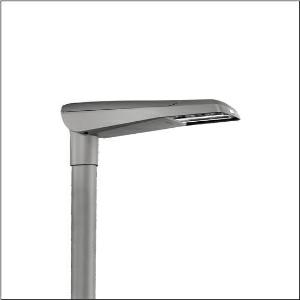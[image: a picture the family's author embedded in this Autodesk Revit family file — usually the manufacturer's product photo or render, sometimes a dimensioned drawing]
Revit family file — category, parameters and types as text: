
# Revit family: streetlight_sl_11_iq_micro___p1_0a_5xc1cc1f08de_50c8
name_source: partatom
category: Lighting Fixtures
units: mm (PartAtom-declared; Revit-internal decimal feet)

## family parameters
Cut with Voids When Loaded = No
Host = Face
Light Source = No
Part Type = Normal
Room Calculation Point = No
Round Connector Dimension = Use Diameter
Shared = No

## types (1)
- --- (1 x LED, 2620 lm, 24.2 W, 2200K)
    Apparent Load = 24 VA
    CIE Flux Codes = 29 63 93 100 100
    Color Rendering = 70
    Color Temperature = 2200K
    Default Elevation = 1800 mm
    Description = Streetlight SL 11 iQ micro, mast luminaire, primary light control with 3 zone facetted reflector, of plastic, silver coated, highly specular, primary optical cover: cover, of PMMA, transparent, light distribution: P1.0a, light emission: direct distribution, primary light characteristic: asymmetric, installation type: post-top, side-entry, lamps: LED, High Power LED, rated values: 3.150lm | 24,1W | 130,7lm/W (begin service life); end service life: 3.150lm | 24,6W; at 50% lumin. flux: 1.575lm | 11,9W | 132,4lm/W, colour temperature: 2200/2700/3000/4000K, colour rendering: CRI > 70, light colour: 722/727/730/740, light setting 1 begin service life: 100% | 3.150lm | 24,1W | 130,7lm/W | 3.000K, light setting 1 end service life: 24,6W, further light settings possible, control: Street-Remote, Auto-Match, Temp-Guard, Lumen-Switch, Night-Set, Smart-Wire, Light-Fading, Desk-Remote (wireless, voltage-free reading and setting of iQ features in the workshop via application-optimized NFC function/RFID function), optimised constant luminous flux control (CLO 2.0), with cable H07RN-F 3x 1.5mm², mains connection: 220..240V, AC, 50/60Hz, connection cable pre-assembled, cable length: 6,5m, luminaire housing, of diecast aluminium, powder-coated, SITECO metallic grey (DB 702S), please order mast flange separately, inclination adjustable without tools: 0°, 5°, 10°, 15° (post-top) | 0°, -5°, -10°, -15° (side-entry), sealing non-destructively replaceable, multi-level sealing system, length: 600mm, width: 174mm, height: 116mm, mast flange for spigot size: 42mm (side-entry): 5XC10008XM4, 60/48mm (side-entry/post-top): 5XC10108XM2, 76/60mm (side-entry/post-top): 5XC10108XM1, equipment: Power, protection rating (complete): IP66, insulation class (complete): insulation class II (safety insulation), certification: CE, ENEC, ENEC+, VDE, impact resistance: IK10, permissible operating ambient temperature for outdoor applications: -25..+50°C, standard-compliant lighting for roads and squares, Environmental Product Declaration (EPD) tested and certified by an independent institute, packaging unit: 1 piece

Light Distribution: P1.0a
    Height = 116 mm
    Lamp = 1 x LED
    Lamp Light Flux = 2620 lm
    Lamp Power = 24.2 W
    Lamp count = 1
    Length = 600 mm
    Luminous efficacy = 108 lm/W
    Manufacturer = Siteco
    ModVariant = No
    Model = 5XC1CC1F08DE
    Mounting Place = Pole
    Mounting Type = Pole top
    Number of Poles = 1
    OnlyDefault = Yes
    Power Factor = 1
    Product Name = Streetlight SL 11 iQ micro | P1.0a
    Product group = mast luminaire | pylon top
    ProductGroupID = 6100
    Protection Class = Protection class II
    Protection Degree = IP 66
    RLX_Detail_Level = 1
    RLX_Emergency_Light_Flux = 0 lm
    RLX_Emergency_Type = 0
    RLX_Emergency_Type_DB = No
    RlxData = <blob elided: 59305 chars, md5=d243c848>
    Socket = socket
    Standby Power = 0 W
    System Light Flux = 2620 lm
    System Power = 24 W
    Type Comments = individual setting: luminous flux: 100 % | dim-lin: 254 | 644 mA
    Type Image = l_1006566.jpg
    URL = http://relux.com
    VarID = @adj_046007
    Voltage = 0 V
    Weight = 0.00 kg
    Width = 174 mm

## geometry (parser evidence)
native form markers: Blend x4, Sweep x13
no freeform markers — native parametric forms only
